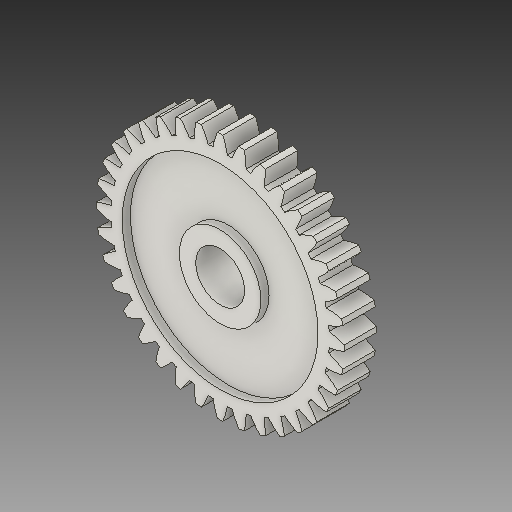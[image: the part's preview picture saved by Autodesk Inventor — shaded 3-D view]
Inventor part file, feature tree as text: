
AUTODESK INVENTOR PART (.ipt)
format: ipt  version: 2019 (Build 230136000, 136)  size: 304,640 bytes
history: imported  units: mm
features: imported_body x1
ambient origin geometry x8: Origin, YZ Plane, XZ Plane, XY Plane, X Axis, Y Axis, Z Axis, Center Point
bodies: Solide1 (imported_parasolid), Solid1 (imported_parasolid)
feature tree (1):
  imported_body  NMx_Import_Brep_tag  [imported B-rep: ~155 faces, bbox_mm=[30.392766, 30.392766, 8.8]]
